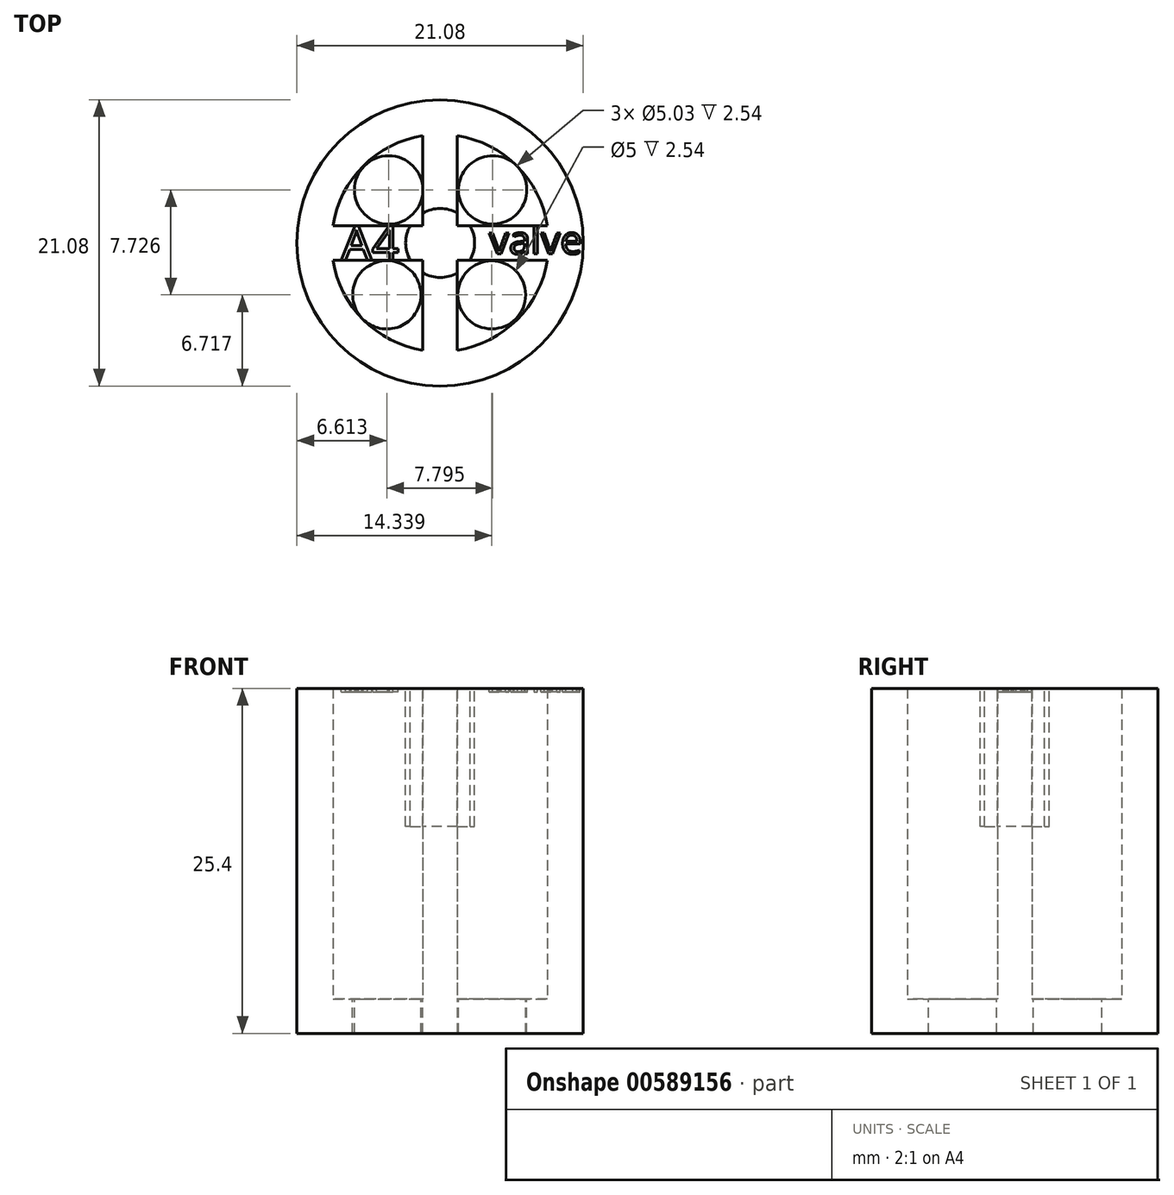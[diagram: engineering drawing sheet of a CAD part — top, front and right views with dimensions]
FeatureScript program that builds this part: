
annotation { "Feature Type Name" : "Feature", "Feature Type Description" : "" }
export const myFeature = defineFeature(function(context is Context, id is Id, definition is map)
    precondition{}
    {
        {
            var Q0;
            Q0=qCreatedBy(makeId("Top.planeOp"),FACE);
            var sketch = newSketch(context, id + "F0", { "sketchPlane" : qUnion([Q0])});
            skCircle(sketch, "E0", {"center": v(0, 0) * mm, "radius": 10.54 * mm});
            skSolve(sketch);
        }
        {
            var Q0;
            Q0=qSketchRegion(id+"F0",true);
            extrude(context, id + "F1", {"entities" : qUnion([Q0]), "depth" : 25.4 * mm, "offsetDistance" : 25.4 * mm});
        }
        {
            var Q0;
            Q0=makeQuery(id+"F1.opExtrude","CAP_FACE",FACE,{"disambiguationData":[OSD([sQuery(id+"F0.wireOp",EDGE,"E0")])],"isStart":false});
            var sketch = newSketch(context, id + "F2", { "sketchPlane" : qUnion([Q0])});
            skCircle(sketch, "E1", {"center": v(0, 0) * mm, "radius": 8 * mm});
            skSolve(sketch);
        }
        {
            var Q0;
            Q0=qSketchRegion(id+"F2",true);
            extrude(context, id + "F3", {"entities" : qUnion([Q0]), "operationType" : NewBodyOperationType.REMOVE, "oppositeDirection" : true, "depth" : 22.86 * mm, "offsetDistance" : 25.4 * mm});
        }
        {
            var Q0;
            Q0=makeQuery(id+"F3.boolean.opBoolean","COPY",FACE,{"derivedFrom":makeQuery(id+"F3.opExtrude","CAP_FACE",FACE,{"disambiguationData":[OSD([sQuery(id+"F2.wireOp",EDGE,"E1")])],"isStart":false})});
            var sketch = newSketch(context, id + "F4", { "sketchPlane" : qUnion([Q0])});
            skLineSegment(sketch, "E2", {"start": v(-1.27, -7.9) * mm, "end": v(-1.27, 7.9) * mm});
            skLineSegment(sketch, "E3", {"start": v(1.27, -7.9) * mm, "end": v(1.27, 7.9) * mm});
            skLineSegment(sketch, "E4", {"start": v(-7.9, 1.27) * mm, "end": v(7.9, 1.27) * mm});
            skLineSegment(sketch, "E5", {"start": v(-7.9, -1.27) * mm, "end": v(7.9, -1.27) * mm});
            skSolve(sketch);
        }
        {
            var Q0;
            Q0=qSketchRegion(id+"F4",true);
            var Q1;
            {var subQ0=sQuery(id+"F4.wireOp",EDGE,"E5");var subQ1=sQuery(id+"F4.wireOp",EDGE,"E3");var subQ2=makeQuery(id+"F4.imprint","INTERSECT",VERTEX,{"derivedFrom":[subQ1,subQ0]});Q1=makeQuery(id+"F4.imprint","IMPRINT",FACE,{"disambiguationData":[TD([[makeQuery(id+"F4.imprint","IMPRINT",EDGE,{"disambiguationData":[TD([[subQ2,-1.0]])],"derivedFrom":subQ1}),-1.0]])]});}
            var Q2;
            {var subQ0=sQuery(id+"F4.wireOp",EDGE,"E2");var subQ1=makeQuery(id+"F3.boolean.opBoolean","COPY",EDGE,{"derivedFrom":makeQuery(id+"F3.opExtrude","CAP_EDGE",EDGE,{"disambiguationData":[OSD([sQuery(id+"F2.wireOp",EDGE,"E1")])],"isStart":false})});var subQ2=makeQuery(id+"F4.imprint","INTERSECT",VERTEX,{"disambiguationData":[OD(1.0)],"derivedFrom":[subQ1,subQ0]});Q2=makeQuery(id+"F4.imprint","IMPRINT",FACE,{"disambiguationData":[TD([[makeQuery(id+"F4.imprint","IMPRINT",EDGE,{"disambiguationData":[TD([[subQ2,1.0]])],"derivedFrom":subQ0}),-1.0]])]});}
            var Q3;
            {var subQ0=sQuery(id+"F4.wireOp",EDGE,"E5");var subQ1=sQuery(id+"F4.wireOp",EDGE,"E2");var subQ2=makeQuery(id+"F4.imprint","INTERSECT",VERTEX,{"derivedFrom":[subQ1,subQ0]});Q3=makeQuery(id+"F4.imprint","IMPRINT",FACE,{"disambiguationData":[TD([[makeQuery(id+"F4.imprint","IMPRINT",EDGE,{"disambiguationData":[TD([[subQ2,-1.0]])],"derivedFrom":subQ1}),1.0]])]});}
            var Q4;
            {var subQ0=sQuery(id+"F4.wireOp",EDGE,"E2");var subQ1=makeQuery(id+"F3.boolean.opBoolean","COPY",EDGE,{"derivedFrom":makeQuery(id+"F3.opExtrude","CAP_EDGE",EDGE,{"disambiguationData":[OSD([sQuery(id+"F2.wireOp",EDGE,"E1")])],"isStart":false})});var subQ2=makeQuery(id+"F4.imprint","INTERSECT",VERTEX,{"disambiguationData":[OD(0.0)],"derivedFrom":[subQ1,subQ0]});Q4=makeQuery(id+"F4.imprint","IMPRINT",FACE,{"disambiguationData":[TD([[makeQuery(id+"F4.imprint","IMPRINT",EDGE,{"disambiguationData":[TD([[subQ2,-1.0]])],"derivedFrom":subQ0}),-1.0]])]});}
            extrude(context, id + "F5", {"entities" : qUnion([Q0, Q1, Q2, Q3, Q4]), "operationType" : NewBodyOperationType.ADD, "depth" : 22.86 * mm, "offsetDistance" : 25.4 * mm});
        }
        {
            var Q0;
            Q0=makeQuery(id+"F5.boolean.opBoolean","MERGE",FACE,{"derivedFrom":[makeQuery(id+"F1.opExtrude","CAP_FACE",FACE,{"disambiguationData":[OSD([sQuery(id+"F0.wireOp",EDGE,"E0")])],"isStart":false}),makeQuery(id+"F5.opExtrude","CAP_FACE",FACE,{"disambiguationData":[OSD([sQuery(id+"F2.wireOp",EDGE,"E1"),sQuery(id+"F4.wireOp",EDGE,"E2"),sQuery(id+"F4.wireOp",EDGE,"E3"),sQuery(id+"F4.wireOp",EDGE,"E4"),sQuery(id+"F4.wireOp",EDGE,"E5")])],"isStart":false})]});
            var sketch = newSketch(context, id + "F6", { "sketchPlane" : qUnion([Q0])});
            skCircle(sketch, "E6", {"center": v(0, 0) * mm, "radius": 2.54 * mm});
            skSolve(sketch);
        }
        {
            var Q0;
            Q0=qSketchRegion(id+"F6",true);
            extrude(context, id + "F7", {"entities" : qUnion([Q0]), "operationType" : NewBodyOperationType.REMOVE, "oppositeDirection" : true, "depth" : 10.16 * mm, "offsetDistance" : 25.4 * mm});
        }
        {
            var Q0;
            {var subQ0=sQuery(id+"F2.wireOp",EDGE,"E1");var subQ1=sQuery(id+"F4.wireOp",EDGE,"E2");var subQ2=makeQuery(id+"F3.boolean.opBoolean","COPY",EDGE,{"derivedFrom":makeQuery(id+"F3.opExtrude","CAP_EDGE",EDGE,{"disambiguationData":[OSD([subQ0])],"isStart":false})});Q0=makeQuery(id+"F5.boolean.opBoolean","SPLIT",FACE,{"disambiguationData":[TD([makeQuery(id+"F5.opExtrude","SWEPT_FACE",FACE,{"disambiguationData":[OSD([subQ1]),TDD([makeQuery(id+"F4.imprint","IMPRINT",EDGE,{"disambiguationData":[TD([[makeQuery(id+"F4.imprint","INTERSECT",VERTEX,{"disambiguationData":[OD(0.0)],"derivedFrom":[subQ2,subQ1]}),-1.0]])],"derivedFrom":subQ1})])]})])],"derivedFrom":makeQuery(id+"F3.boolean.opBoolean","COPY",FACE,{"derivedFrom":makeQuery(id+"F3.opExtrude","CAP_FACE",FACE,{"disambiguationData":[OSD([subQ0])],"isStart":false})})});}
            var sketch = newSketch(context, id + "F8", { "sketchPlane" : qUnion([Q0])});
            skCircle(sketch, "E7", {"center": v(-3.93, -3.82) * mm, "radius": 2.51 * mm});
            skCircle(sketch, "E8", {"center": v(-3.79, 3.9) * mm, "radius": 2.51 * mm});
            skCircle(sketch, "E9", {"center": v(3.87, 3.9) * mm, "radius": 2.51 * mm});
            skCircle(sketch, "E10", {"center": v(3.8, -3.82) * mm, "radius": 2.5 * mm});
            skSolve(sketch);
        }
        {
            var Q0;
            Q0=makeQuery(id+"F8.imprint","IMPRINT",FACE,{"disambiguationData":[TD([[makeQuery(id+"F8.imprint","IMPRINT",EDGE,{"derivedFrom":sQuery(id+"F8.wireOp",EDGE,"E8")}),1.0]])]});
            var Q1;
            Q1=makeQuery(id+"F8.imprint","IMPRINT",FACE,{"disambiguationData":[TD([[makeQuery(id+"F8.imprint","IMPRINT",EDGE,{"derivedFrom":sQuery(id+"F8.wireOp",EDGE,"E9")}),1.0]])]});
            var Q2;
            Q2=makeQuery(id+"F8.imprint","IMPRINT",FACE,{"disambiguationData":[TD([[makeQuery(id+"F8.imprint","IMPRINT",EDGE,{"derivedFrom":sQuery(id+"F8.wireOp",EDGE,"E10")}),1.0]])]});
            var Q3;
            Q3=makeQuery(id+"F8.imprint","IMPRINT",FACE,{"disambiguationData":[TD([[makeQuery(id+"F8.imprint","IMPRINT",EDGE,{"derivedFrom":sQuery(id+"F8.wireOp",EDGE,"E7")}),1.0]])]});
            extrude(context, id + "F9", {"entities" : qUnion([Q0, Q1, Q2, Q3]), "operationType" : NewBodyOperationType.REMOVE, "endBound" : BoundingType.THROUGH_ALL, "oppositeDirection" : true, "depth" : 25.4 * mm, "offsetDistance" : 25.4 * mm});
        }
        {
            var Q0;
            Q0=makeQuery(id+"F5.boolean.opBoolean","MERGE",FACE,{"derivedFrom":[makeQuery(id+"F1.opExtrude","CAP_FACE",FACE,{"disambiguationData":[OSD([sQuery(id+"F0.wireOp",EDGE,"E0")])],"isStart":false}),makeQuery(id+"F5.opExtrude","CAP_FACE",FACE,{"disambiguationData":[OSD([sQuery(id+"F2.wireOp",EDGE,"E1"),sQuery(id+"F4.wireOp",EDGE,"E2"),sQuery(id+"F4.wireOp",EDGE,"E3"),sQuery(id+"F4.wireOp",EDGE,"E4"),sQuery(id+"F4.wireOp",EDGE,"E5")])],"isStart":false})]});
            var sketch = newSketch(context, id + "F10", { "sketchPlane" : qUnion([Q0])});
            skText(sketch, "E11", { "text": "A4", "fontName": "OpenSans-Regular.ttf"});
            const initialGuessF10  = {"E11": [-0.00727, -0.00127, 1, 0, 0.00254]};
            skSetInitialGuess(sketch, initialGuessF10);
            skSolve(sketch);
        }
        {
            var Q0;
            Q0 = qSketchRegion(id + "F10", true);
            extrude(context, id + "F11", {"entities" : qUnion([Q0]), "operationType" : NewBodyOperationType.REMOVE, "oppositeDirection" : true, "depth" : 0.25 * mm, "offsetDistance" : 25.4 * mm});
        }
        {
            var Q0;
            {var subQ0=sQuery(id+"F4.wireOp",EDGE,"E5");var subQ1=sQuery(id+"F2.wireOp",EDGE,"E1");var subQ3=sQuery(id+"F4.wireOp",EDGE,"E3");var subQ7=sQuery(id+"F4.wireOp",EDGE,"E4");var subQ8=sQuery(id+"F4.wireOp",EDGE,"E2");var subQ9=makeQuery(id+"F5.opExtrude","CAP_FACE",FACE,{"disambiguationData":[OSD([subQ1,subQ8,subQ3,subQ7,subQ0])],"isStart":false});var subQ12=sQuery(id+"F0.wireOp",EDGE,"E0");var subQ13=makeQuery(id+"F1.opExtrude","CAP_FACE",FACE,{"disambiguationData":[OSD([subQ12])],"isStart":false});Q0=makeQuery(id+"F11.boolean.opBoolean","SPLIT",FACE,{"disambiguationData":[TD([makeQuery(id+"F1.opExtrude","SWEPT_FACE",FACE,{"disambiguationData":[OSD([subQ12])]})])],"derivedFrom":makeQuery(id+"F5.boolean.opBoolean","MERGE",FACE,{"derivedFrom":[subQ13,subQ9]})});}
            var sketch = newSketch(context, id + "F12", { "sketchPlane" : qUnion([Q0])});
            skText(sketch, "E12", { "text": "valve", "fontName": "OpenSans-Regular.ttf"});
            const initialGuessF12  = {"E12": [0.00362, -0.00081, 1, 0, 0.00208]};
            skSetInitialGuess(sketch, initialGuessF12);
            skSolve(sketch);
        }
        {
            var Q0;
            Q0 = qSketchRegion(id + "F12", true);
            extrude(context, id + "F13", {"entities" : qUnion([Q0]), "operationType" : NewBodyOperationType.REMOVE, "oppositeDirection" : true, "depth" : 0.25 * mm, "offsetDistance" : 25.4 * mm});
        }
    });
